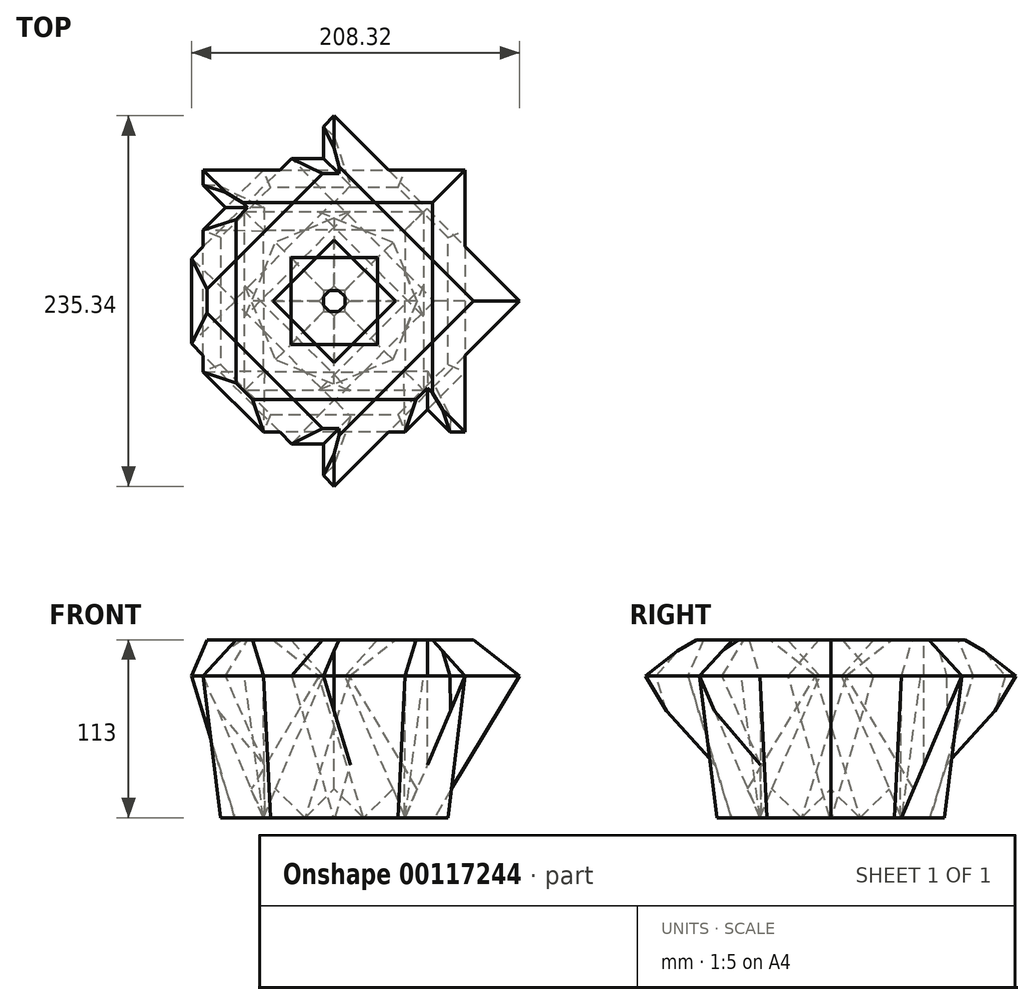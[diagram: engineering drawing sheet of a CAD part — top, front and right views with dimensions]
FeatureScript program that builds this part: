
annotation { "Feature Type Name" : "Feature", "Feature Type Description" : "" }
export const myFeature = defineFeature(function(context is Context, id is Id, definition is map)
    precondition{}
    {
        {
            var Q0;
            Q0=qCreatedBy(makeId("Top.planeOp"),FACE);
            var sketch = newSketch(context, id + "F0", { "sketchPlane" : qUnion([Q0])});
            skLineSegment(sketch, "E0.bottom", {"start": v(45, -45) * mm, "end": v(-45, -45) * mm});
            skLineSegment(sketch, "E0.top", {"start": v(45, 45) * mm, "end": v(-45, 45) * mm});
            skLineSegment(sketch, "E0.left", {"start": v(45, -45) * mm, "end": v(45, 45) * mm});
            skLineSegment(sketch, "E0.right", {"start": v(-45, -45) * mm, "end": v(-45, 45) * mm});
            skPoint(sketch, "E0.middle", {"position": v(0, 0) * mm});
            skCircle(sketch, "E1.cCircle", {"center": v(0, 0) * mm, "radius": 45 * mm, "construction": true});
            skLineSegment(sketch, "E1.0", {"start": v(-45, -18.64) * mm, "end": v(-45, 18.64) * mm});
            skLineSegment(sketch, "E1.1", {"start": v(-45, 18.64) * mm, "end": v(-18.64, 45) * mm});
            skLineSegment(sketch, "E1.2", {"start": v(-18.64, 45) * mm, "end": v(18.64, 45) * mm});
            skLineSegment(sketch, "E1.3", {"start": v(18.64, 45) * mm, "end": v(45, 18.64) * mm});
            skLineSegment(sketch, "E1.4", {"start": v(45, 18.64) * mm, "end": v(45, -18.64) * mm});
            skLineSegment(sketch, "E1.5", {"start": v(45, -18.64) * mm, "end": v(18.64, -45) * mm});
            skLineSegment(sketch, "E1.6", {"start": v(18.64, -45) * mm, "end": v(-18.64, -45) * mm});
            skLineSegment(sketch, "E1.7", {"start": v(-18.64, -45) * mm, "end": v(-45, -18.64) * mm});
            skPoint(sketch, "E1.0.midPoint", {"position": v(-45, 0) * mm});
            skSolve(sketch);
        }
        {
            var Q0;
            Q0=qCreatedBy(makeId("Front.planeOp"),FACE);
            var sketch = newSketch(context, id + "F1", { "sketchPlane" : qUnion([Q0])});
            skLineSegment(sketch, "E2", {"start": v(0, 0) * mm, "end": v(0, 72.67) * mm});
            skSolve(sketch);
        }
        {
            var Q0;
            Q0=makeQuery(id+"F0.imprint","IMPRINT",FACE,{"disambiguationData":[TD([[makeQuery(id+"F0.imprint","IMPRINT",EDGE,{"derivedFrom":sQuery(id+"F0.wireOp",EDGE,"E0.bottom")}),-1.0]])]});
            var Q1;
            {var subQ3=sQuery(id+"F0.wireOp",EDGE,"E1.3");Q1=makeQuery(id+"F0.imprint","IMPRINT",FACE,{"disambiguationData":[TD([[makeQuery(id+"F0.imprint","IMPRINT",EDGE,{"derivedFrom":subQ3}),1.0]])]});}
            var Q2;
            {var subQ3=sQuery(id+"F0.wireOp",EDGE,"E1.1");Q2=makeQuery(id+"F0.imprint","IMPRINT",FACE,{"disambiguationData":[TD([[makeQuery(id+"F0.imprint","IMPRINT",EDGE,{"derivedFrom":subQ3}),1.0]])]});}
            var Q3;
            Q3=makeQuery(id+"F0.imprint","IMPRINT",FACE,{"disambiguationData":[TD([[makeQuery(id+"F0.imprint","IMPRINT",EDGE,{"derivedFrom":sQuery(id+"F0.wireOp",EDGE,"E1.0")}),-1.0]])]});
            extrude(context, id + "F2", {"entities" : qUnion([Q0, Q1, Q2, Q3]), "depth" : 90 * mm, "hasDraft" : true, "draftAngle" : 23 * degree});
        }
        {
            var Q0;
            Q0=makeQuery(id+"F2.opExtrude","CAP_FACE",FACE,{"disambiguationData":[OSD([sQuery(id+"F0.wireOp",EDGE,"E0.bottom"),sQuery(id+"F0.wireOp",EDGE,"E0.top"),sQuery(id+"F0.wireOp",EDGE,"E0.left"),sQuery(id+"F0.wireOp",EDGE,"E0.right")])],"isStart":false});
            var sketch = newSketch(context, id + "F3", { "sketchPlane" : qUnion([Q0])});
            skLineSegment(sketch, "E3", {"start": v(-83.2, 45) * mm, "end": v(-45, 83.2) * mm});
            skLineSegment(sketch, "E4", {"start": v(-45, 83.2) * mm, "end": v(45, 83.2) * mm});
            skLineSegment(sketch, "E5", {"start": v(45, 83.2) * mm, "end": v(83.2, 45) * mm});
            skLineSegment(sketch, "E6", {"start": v(83.2, 45) * mm, "end": v(83.2, -45) * mm});
            skLineSegment(sketch, "E7", {"start": v(83.2, -45) * mm, "end": v(45, -83.2) * mm});
            skLineSegment(sketch, "E8", {"start": v(-45, -83.2) * mm, "end": v(-83.2, -45) * mm});
            skLineSegment(sketch, "E9", {"start": v(-83.2, -45) * mm, "end": v(-83.2, 45) * mm});
            skLineSegment(sketch, "E10", {"start": v(-45, -83.2) * mm, "end": v(45, -83.2) * mm});
            skPoint(sketch, "E11", {"position": v(-83.2, 0) * mm});
            skPoint(sketch, "E12", {"position": v(0, 83.2) * mm});
            skSolve(sketch);
        }
        {
            var Q0;
            Q0=makeQuery(id+"F2.opExtrude","CAP_FACE",FACE,{"disambiguationData":[OSD([sQuery(id+"F0.wireOp",EDGE,"E0.bottom"),sQuery(id+"F0.wireOp",EDGE,"E0.top"),sQuery(id+"F0.wireOp",EDGE,"E0.left"),sQuery(id+"F0.wireOp",EDGE,"E0.right")])],"isStart":false});
            extrude(context, id + "F4", {"entities" : qUnion([Q0]), "operationType" : NewBodyOperationType.ADD, "depth" : 23 * mm, "hasDraft" : true, "draftAngle" : 42 * degree, "draftPullDirection" : true});
        }
        {
            var Q0;
            {var subQ0=sQuery(id+"F3.wireOp",EDGE,"E5");Q0=makeQuery(id+"F3.imprint","IMPRINT",FACE,{"disambiguationData":[TD([[makeQuery(id+"F3.imprint","IMPRINT",EDGE,{"derivedFrom":subQ0}),1.0]])]});}
            var Q1;
            {var subQ0=sQuery(id+"F3.wireOp",EDGE,"E7");Q1=makeQuery(id+"F3.imprint","IMPRINT",FACE,{"disambiguationData":[TD([[makeQuery(id+"F3.imprint","IMPRINT",EDGE,{"derivedFrom":subQ0}),1.0]])]});}
            var Q2;
            {var subQ0=sQuery(id+"F3.wireOp",EDGE,"E8");Q2=makeQuery(id+"F3.imprint","IMPRINT",FACE,{"disambiguationData":[TD([[makeQuery(id+"F3.imprint","IMPRINT",EDGE,{"derivedFrom":subQ0}),1.0]])]});}
            var Q3;
            {var subQ0=sQuery(id+"F3.wireOp",EDGE,"E3");Q3=makeQuery(id+"F3.imprint","IMPRINT",FACE,{"disambiguationData":[TD([[makeQuery(id+"F3.imprint","IMPRINT",EDGE,{"derivedFrom":subQ0}),1.0]])]});}
            extrude(context, id + "F5", {"entities" : qUnion([Q0, Q1, Q2, Q3]), "operationType" : NewBodyOperationType.REMOVE, "oppositeDirection" : true, "depth" : 90 * mm, "hasDraft" : true, "draftAngle" : 17 * degree, "hasSecondDirection" : true, "secondDirectionOppositeDirection" : false, "secondDirectionDepth" : 25 * mm, "hasSecondDirectionDraft" : true, "secondDirectionDraftAngle" : 23 * degree});
        }
        {
            var Q0;
            Q0=makeQuery(id+"F3.imprint","IMPRINT",FACE,{"disambiguationData":[TD([[makeQuery(id+"F3.imprint","IMPRINT",EDGE,{"derivedFrom":sQuery(id+"F3.wireOp",EDGE,"E3")}),-1.0]])]});
            extrude(context, id + "F6", {"entities" : qUnion([Q0]), "oppositeDirection" : true, "depth" : 90 * mm, "hasDraft" : true, "draftAngle" : 7 * degree, "draftPullDirection" : true});
        }
        {
            var Q0;
            Q0=makeQuery(id+"F2.opExtrude","SWEPT_BODY",BODY,{"disambiguationData":[OSD([sQuery(id+"F0.wireOp",EDGE,"E0.bottom"),sQuery(id+"F0.wireOp",EDGE,"E0.top"),sQuery(id+"F0.wireOp",EDGE,"E0.left"),sQuery(id+"F0.wireOp",EDGE,"E0.right"),sQuery(id+"F0.wireOp",EDGE,"E1.0"),sQuery(id+"F0.wireOp",EDGE,"E1.2"),sQuery(id+"F0.wireOp",EDGE,"E1.4"),sQuery(id+"F0.wireOp",EDGE,"E1.6")])]});
            transform(context, id + "F7", {"entities" : qUnion([Q0]), "transformType" : TransformType.COPY});
        }
        {
            var Q0;
            Q0=makeQuery(id+"F7.opPattern","COPY",BODY,{"derivedFrom":makeQuery(id+"F2.opExtrude","SWEPT_BODY",BODY,{"disambiguationData":[OSD([sQuery(id+"F0.wireOp",EDGE,"E0.bottom"),sQuery(id+"F0.wireOp",EDGE,"E0.top"),sQuery(id+"F0.wireOp",EDGE,"E0.left"),sQuery(id+"F0.wireOp",EDGE,"E0.right"),sQuery(id+"F0.wireOp",EDGE,"E1.0"),sQuery(id+"F0.wireOp",EDGE,"E1.2"),sQuery(id+"F0.wireOp",EDGE,"E1.4"),sQuery(id+"F0.wireOp",EDGE,"E1.6")])]}),"instanceName":"1"});
            var Q1;
            Q1=sQuery(id+"F1.wireOp",EDGE,"E2");
            transform(context, id + "F8", {"entities" : qUnion([Q0]), "transformType" : TransformType.ROTATION, "transformAxis" : qUnion([Q1]), "angle" : 45 * degree, "oppositeDirection" : true, "makeCopy" : false});
        }
        {
            var Q0;
            {var subQ3=sQuery(id+"F0.wireOp",EDGE,"E1.7");Q0=makeQuery(id+"F0.imprint","IMPRINT",FACE,{"disambiguationData":[TD([[makeQuery(id+"F0.imprint","IMPRINT",EDGE,{"derivedFrom":subQ3}),1.0]])]});}
            var Q1;
            Q1=makeQuery(id+"F0.imprint","IMPRINT",FACE,{"disambiguationData":[TD([[makeQuery(id+"F0.imprint","IMPRINT",EDGE,{"derivedFrom":sQuery(id+"F0.wireOp",EDGE,"E1.0")}),-1.0]])]});
            var Q2;
            {var subQ3=sQuery(id+"F0.wireOp",EDGE,"E1.1");Q2=makeQuery(id+"F0.imprint","IMPRINT",FACE,{"disambiguationData":[TD([[makeQuery(id+"F0.imprint","IMPRINT",EDGE,{"derivedFrom":subQ3}),1.0]])]});}
            var Q3;
            {var subQ3=sQuery(id+"F0.wireOp",EDGE,"E1.3");Q3=makeQuery(id+"F0.imprint","IMPRINT",FACE,{"disambiguationData":[TD([[makeQuery(id+"F0.imprint","IMPRINT",EDGE,{"derivedFrom":subQ3}),1.0]])]});}
            var Q4;
            {var subQ3=sQuery(id+"F0.wireOp",EDGE,"E1.5");Q4=makeQuery(id+"F0.imprint","IMPRINT",FACE,{"disambiguationData":[TD([[makeQuery(id+"F0.imprint","IMPRINT",EDGE,{"derivedFrom":subQ3}),1.0]])]});}
            extrude(context, id + "F9", {"entities" : qUnion([Q0, Q1, Q2, Q3, Q4]), "depth" : 90 * mm, "hasDraft" : true, "draftAngle" : 7.5 * degree});
        }
    });
